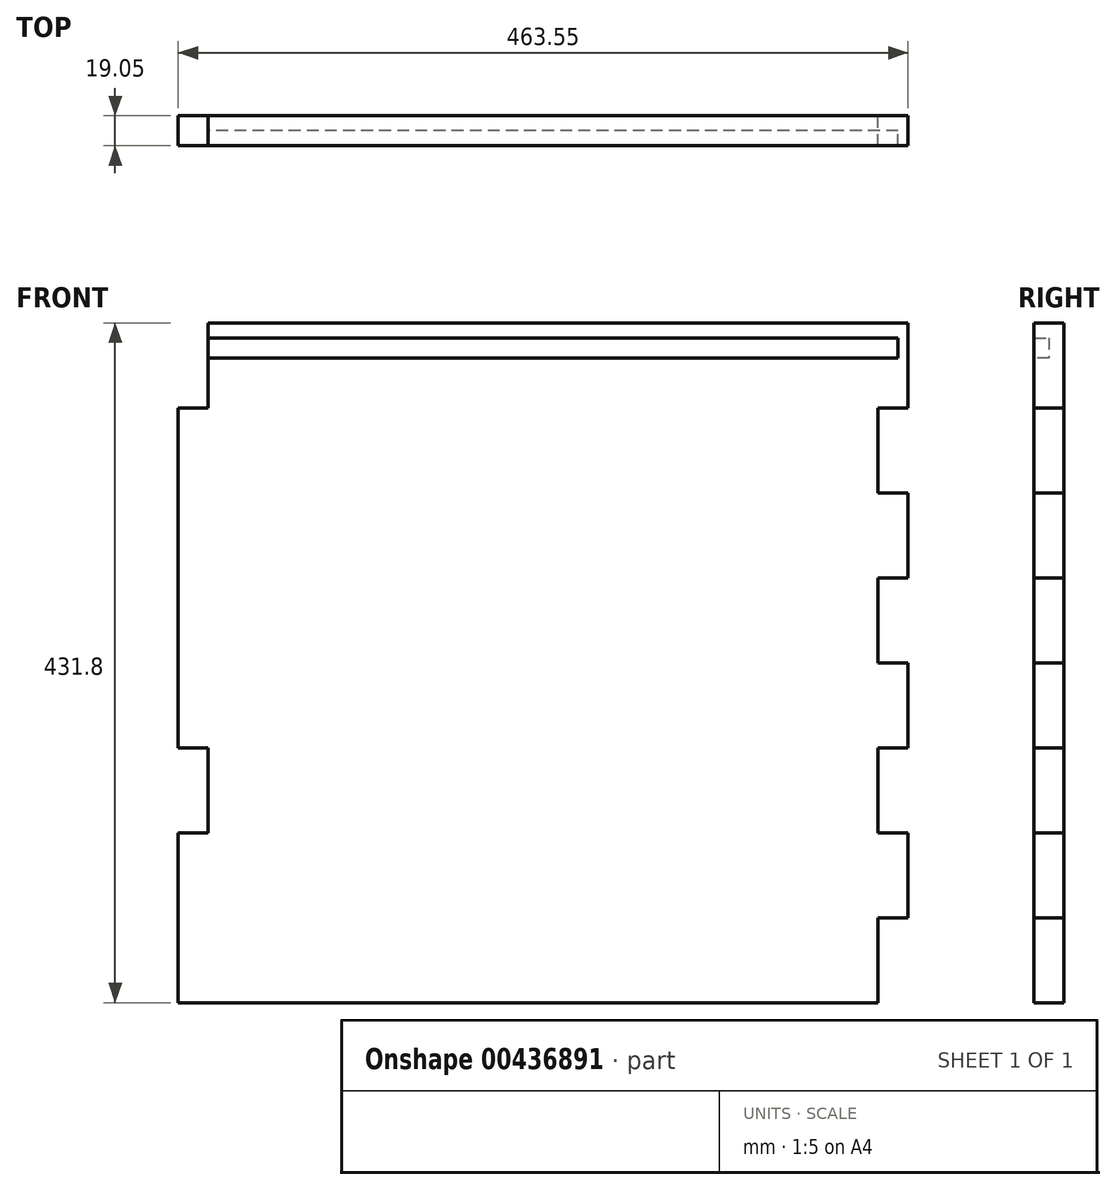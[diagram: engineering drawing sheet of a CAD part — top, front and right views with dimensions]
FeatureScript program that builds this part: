
annotation { "Feature Type Name" : "Feature", "Feature Type Description" : "" }
export const myFeature = defineFeature(function(context is Context, id is Id, definition is map)
    precondition{}
    {
        {
            var Q0;
            Q0=qCreatedBy(makeId("Front.planeOp"),FACE);
            var sketch = newSketch(context, id + "F0", { "sketchPlane" : qUnion([Q0])});
            skLineSegment(sketch, "E0.bottom", {"start": v(0, 0) * mm, "end": v(444.5, 0) * mm});
            skLineSegment(sketch, "E0.top", {"start": v(19.05, 431.8) * mm, "end": v(463.55, 431.8) * mm});
            skLineSegment(sketch, "E1", {"start": v(463.55, 431.8) * mm, "end": v(463.55, 377.83) * mm});
            skLineSegment(sketch, "E2", {"start": v(463.55, 377.83) * mm, "end": v(444.5, 377.83) * mm});
            skLineSegment(sketch, "E3", {"start": v(444.5, 377.83) * mm, "end": v(444.5, 323.85) * mm});
            skLineSegment(sketch, "E4", {"start": v(444.5, 323.85) * mm, "end": v(463.55, 323.85) * mm});
            skLineSegment(sketch, "E5", {"start": v(463.55, 323.85) * mm, "end": v(463.55, 269.88) * mm});
            skLineSegment(sketch, "E6", {"start": v(463.55, 269.88) * mm, "end": v(444.5, 269.88) * mm});
            skLineSegment(sketch, "E7", {"start": v(444.5, 269.88) * mm, "end": v(444.5, 215.9) * mm});
            skLineSegment(sketch, "E8", {"start": v(444.5, 215.9) * mm, "end": v(463.55, 215.9) * mm});
            skLineSegment(sketch, "E9", {"start": v(463.55, 215.9) * mm, "end": v(463.55, 161.93) * mm});
            skLineSegment(sketch, "E10", {"start": v(463.55, 161.93) * mm, "end": v(444.5, 161.93) * mm});
            skLineSegment(sketch, "E11", {"start": v(444.5, 161.93) * mm, "end": v(444.5, 107.95) * mm});
            skLineSegment(sketch, "E12", {"start": v(444.5, 107.95) * mm, "end": v(463.55, 107.95) * mm});
            skLineSegment(sketch, "E13", {"start": v(463.55, 107.95) * mm, "end": v(463.55, 53.98) * mm});
            skLineSegment(sketch, "E14", {"start": v(463.55, 53.98) * mm, "end": v(444.5, 53.98) * mm});
            skLineSegment(sketch, "E15", {"start": v(444.5, 53.98) * mm, "end": v(444.5, 0) * mm});
            skLineSegment(sketch, "E16", {"start": v(19.05, 431.8) * mm, "end": v(19.05, 377.83) * mm});
            skLineSegment(sketch, "E17", {"start": v(19.05, 377.83) * mm, "end": v(0, 377.83) * mm});
            skLineSegment(sketch, "E18", {"start": v(0, 0) * mm, "end": v(0, 107.95) * mm});
            skLineSegment(sketch, "E19", {"start": v(0, 107.95) * mm, "end": v(19.05, 107.95) * mm});
            skLineSegment(sketch, "E20", {"start": v(19.05, 107.95) * mm, "end": v(19.05, 161.93) * mm});
            skLineSegment(sketch, "E21", {"start": v(19.05, 161.93) * mm, "end": v(0, 161.93) * mm});
            skLineSegment(sketch, "E22", {"start": v(0, 161.93) * mm, "end": v(0, 377.83) * mm});
            skSolve(sketch);
        }
        {
            var Q0;
            Q0=makeQuery(id+"F0.imprint","IMPRINT",FACE,{"disambiguationData":[TD([[makeQuery(id+"F0.imprint","IMPRINT",EDGE,{"derivedFrom":sQuery(id+"F0.wireOp",EDGE,"E0.bottom")}),1.0]])]});
            extrude(context, id + "F1", {"entities" : qUnion([Q0]), "depth" : 19.05 * mm});
        }
        {
            var Q0;
            Q0=makeQuery(id+"F1.opExtrude","SWEPT_FACE",FACE,{"disambiguationData":[OSD([sQuery(id+"F0.wireOp",EDGE,"E16")])]});
            var sketch = newSketch(context, id + "F2", { "sketchPlane" : qUnion([Q0])});
            skLineSegment(sketch, "E23", {"start": v(19.05, 422.28) * mm, "end": v(9.52, 422.28) * mm});
            skLineSegment(sketch, "E24", {"start": v(9.52, 422.28) * mm, "end": v(9.52, 409.58) * mm});
            skLineSegment(sketch, "E25", {"start": v(9.52, 409.58) * mm, "end": v(19.05, 409.58) * mm});
            skSolve(sketch);
        }
        {
            var Q0;
            {var subQ0=sQuery(id+"F2.wireOp",EDGE,"E23");Q0=makeQuery(id+"F2.imprint","IMPRINT",FACE,{"disambiguationData":[TD([[makeQuery(id+"F2.imprint","IMPRINT",EDGE,{"derivedFrom":subQ0}),1.0]])]});}
            extrude(context, id + "F3", {"entities" : qUnion([Q0]), "operationType" : NewBodyOperationType.REMOVE, "oppositeDirection" : true, "depth" : 438.15 * mm});
        }
    });
